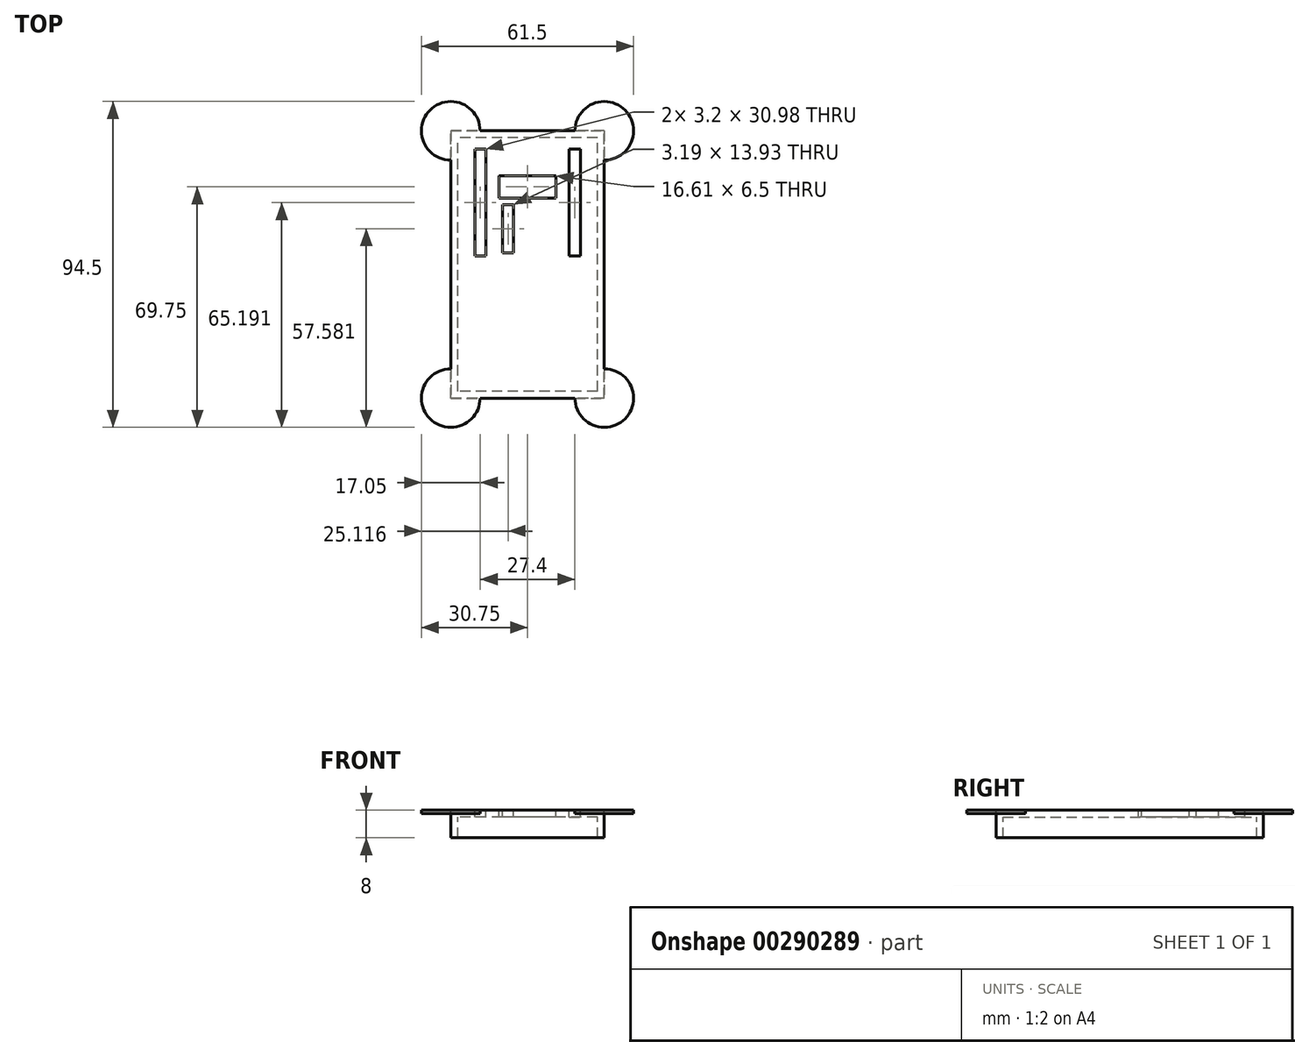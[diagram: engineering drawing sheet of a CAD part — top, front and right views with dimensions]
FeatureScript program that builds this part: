
annotation { "Feature Type Name" : "Feature", "Feature Type Description" : "" }
export const myFeature = defineFeature(function(context is Context, id is Id, definition is map)
    precondition{}
    {
        {
            var Q0;
            Q0=qCreatedBy(makeId("Top.planeOp"),FACE);
            var sketch = newSketch(context, id + "F0", { "sketchPlane" : qUnion([Q0])});
            skLineSegment(sketch, "E0.bottom", {"start": v(20.25, 36.75) * mm, "end": v(-20.25, 36.75) * mm});
            skLineSegment(sketch, "E0.top", {"start": v(20.25, -36.75) * mm, "end": v(-20.25, -36.75) * mm});
            skLineSegment(sketch, "E0.left", {"start": v(20.25, 36.75) * mm, "end": v(20.25, -36.75) * mm});
            skLineSegment(sketch, "E0.right", {"start": v(-20.25, 36.75) * mm, "end": v(-20.25, -36.75) * mm});
            skPoint(sketch, "E0.middle", {"position": v(0, 0) * mm});
            skLineSegment(sketch, "E1.bottom", {"start": v(22.25, 38.75) * mm, "end": v(-22.25, 38.75) * mm});
            skLineSegment(sketch, "E1.top", {"start": v(22.25, -38.75) * mm, "end": v(-22.25, -38.75) * mm});
            skLineSegment(sketch, "E1.left", {"start": v(22.25, 38.75) * mm, "end": v(22.25, -38.75) * mm});
            skLineSegment(sketch, "E1.right", {"start": v(-22.25, 38.75) * mm, "end": v(-22.25, -38.75) * mm});
            skLineSegment(sketch, "E2.bottom", {"start": v(17.1, 34.25) * mm, "end": v(-17.1, 34.25) * mm});
            skLineSegment(sketch, "E2.top", {"start": v(17.1, 0.75) * mm, "end": v(-17.1, 0.75) * mm});
            skLineSegment(sketch, "E2.left", {"start": v(17.1, 34.25) * mm, "end": v(17.1, 0.75) * mm});
            skLineSegment(sketch, "E2.right", {"start": v(-17.1, 34.25) * mm, "end": v(-17.1, 0.75) * mm});
            skPoint(sketch, "E2.middle", {"position": v(0, 17.5) * mm});
            skLineSegment(sketch, "E3.bottom", {"start": v(12.1, 33.43) * mm, "end": v(15.3, 33.43) * mm});
            skLineSegment(sketch, "E3.top", {"start": v(12.1, 2.45) * mm, "end": v(15.3, 2.45) * mm});
            skLineSegment(sketch, "E3.left", {"start": v(12.1, 33.43) * mm, "end": v(12.1, 2.45) * mm});
            skLineSegment(sketch, "E3.right", {"start": v(15.3, 33.43) * mm, "end": v(15.3, 2.45) * mm});
            skLineSegment(sketch, "E4", {"start": v(0, 34.25) * mm, "end": v(0, 0.75) * mm, "construction": true});
            skLineSegment(sketch, "E5.MirrorCS", {"start": v(-12.1, 33.43) * mm, "end": v(-12.1, 2.45) * mm});
            skLineSegment(sketch, "E6.MirrorCS", {"start": v(-12.1, 33.43) * mm, "end": v(-15.3, 33.43) * mm});
            skLineSegment(sketch, "E7.MirrorCS", {"start": v(-15.3, 33.43) * mm, "end": v(-15.3, 2.45) * mm});
            skLineSegment(sketch, "E8.MirrorCS", {"start": v(-12.1, 2.45) * mm, "end": v(-15.3, 2.45) * mm});
            skLineSegment(sketch, "E9.bottom", {"start": v(8.3, 25.75) * mm, "end": v(-8.3, 25.75) * mm});
            skLineSegment(sketch, "E9.top", {"start": v(8.3, 19.25) * mm, "end": v(-8.3, 19.25) * mm});
            skLineSegment(sketch, "E9.left", {"start": v(8.3, 25.75) * mm, "end": v(8.3, 19.25) * mm});
            skLineSegment(sketch, "E9.right", {"start": v(-8.3, 25.75) * mm, "end": v(-8.3, 19.25) * mm});
            skPoint(sketch, "E9.middle", {"position": v(0, 22.5) * mm});
            skLineSegment(sketch, "E10.bottom", {"start": v(-4.04, 17.3) * mm, "end": v(-7.23, 17.3) * mm});
            skLineSegment(sketch, "E10.top", {"start": v(-4.04, 3.37) * mm, "end": v(-7.23, 3.37) * mm});
            skLineSegment(sketch, "E10.left", {"start": v(-4.04, 17.3) * mm, "end": v(-4.04, 3.37) * mm});
            skLineSegment(sketch, "E10.right", {"start": v(-7.23, 17.3) * mm, "end": v(-7.23, 3.37) * mm});
            skPoint(sketch, "E10.middle", {"position": v(-5.63, 10.33) * mm});
            skSolve(sketch);
        }
        {
            var Q0;
            Q0=makeQuery(id+"F0.imprint","IMPRINT",FACE,{"disambiguationData":[TD([[makeQuery(id+"F0.imprint","IMPRINT",EDGE,{"derivedFrom":sQuery(id+"F0.wireOp",EDGE,"E0.bottom")}),1.0]])]});
            var Q1;
            Q1=makeQuery(id+"F0.imprint","IMPRINT",FACE,{"disambiguationData":[TD([[makeQuery(id+"F0.imprint","IMPRINT",EDGE,{"derivedFrom":sQuery(id+"F0.wireOp",EDGE,"E0.bottom")}),-1.0]])]});
            var Q2;
            Q2=makeQuery(id+"F0.imprint","IMPRINT",FACE,{"disambiguationData":[TD([[makeQuery(id+"F0.imprint","IMPRINT",EDGE,{"derivedFrom":sQuery(id+"F0.wireOp",EDGE,"E2.bottom")}),1.0]])]});
            extrude(context, id + "F1", {"entities" : qUnion([Q0, Q1, Q2]), "oppositeDirection" : true, "depth" : 2 * mm});
        }
        {
            var Q0;
            Q0=makeQuery(id+"F1.opExtrude","CAP_FACE",FACE,{"disambiguationData":[OSD([sQuery(id+"F0.wireOp",EDGE,"E1.bottom"),sQuery(id+"F0.wireOp",EDGE,"E1.top"),sQuery(id+"F0.wireOp",EDGE,"E1.left"),sQuery(id+"F0.wireOp",EDGE,"E1.right")])],"isStart":false});
            var sketch = newSketch(context, id + "F2", { "sketchPlane" : qUnion([Q0])});
            skLineSegment(sketch, "E11.bottom", {"start": v(-22.25, 38.75) * mm, "end": v(22.25, 38.75) * mm});
            skLineSegment(sketch, "E11.top", {"start": v(-22.25, -38.75) * mm, "end": v(22.25, -38.75) * mm});
            skLineSegment(sketch, "E11.left", {"start": v(-22.25, 38.75) * mm, "end": v(-22.25, -38.75) * mm});
            skLineSegment(sketch, "E11.right", {"start": v(22.25, 38.75) * mm, "end": v(22.25, -38.75) * mm});
            skLineSegment(sketch, "E12.bottom", {"start": v(20.25, 36.75) * mm, "end": v(-20.25, 36.75) * mm});
            skLineSegment(sketch, "E12.top", {"start": v(20.25, -36.75) * mm, "end": v(-20.25, -36.75) * mm});
            skLineSegment(sketch, "E12.left", {"start": v(20.25, 36.75) * mm, "end": v(20.25, -36.75) * mm});
            skLineSegment(sketch, "E12.right", {"start": v(-20.25, 36.75) * mm, "end": v(-20.25, -36.75) * mm});
            skPoint(sketch, "E12.middle", {"position": v(0, 0) * mm});
            skSolve(sketch);
        }
        {
            var Q0;
            Q0=makeQuery(id+"F2.imprint","IMPRINT",FACE,{"disambiguationData":[TD([[makeQuery(id+"F2.imprint","IMPRINT",EDGE,{"derivedFrom":sQuery(id+"F2.wireOp",EDGE,"E11.bottom")}),1.0]])]});
            extrude(context, id + "F3", {"entities" : qUnion([Q0]), "operationType" : NewBodyOperationType.ADD, "depth" : 6 * mm});
        }
        {
            var Q0;
            Q0=makeQuery(id+"F1.opExtrude","CAP_FACE",FACE,{"disambiguationData":[OSD([sQuery(id+"F0.wireOp",EDGE,"E1.bottom"),sQuery(id+"F0.wireOp",EDGE,"E1.top"),sQuery(id+"F0.wireOp",EDGE,"E1.left"),sQuery(id+"F0.wireOp",EDGE,"E1.right"),sQuery(id+"F0.wireOp",EDGE,"E3.bottom"),sQuery(id+"F0.wireOp",EDGE,"E3.top"),sQuery(id+"F0.wireOp",EDGE,"E3.left"),sQuery(id+"F0.wireOp",EDGE,"E3.right"),sQuery(id+"F0.wireOp",EDGE,"E5.MirrorCS"),sQuery(id+"F0.wireOp",EDGE,"E6.MirrorCS"),sQuery(id+"F0.wireOp",EDGE,"E7.MirrorCS"),sQuery(id+"F0.wireOp",EDGE,"E8.MirrorCS"),sQuery(id+"F0.wireOp",EDGE,"E9.bottom"),sQuery(id+"F0.wireOp",EDGE,"E9.top"),sQuery(id+"F0.wireOp",EDGE,"E9.left"),sQuery(id+"F0.wireOp",EDGE,"E9.right"),sQuery(id+"F0.wireOp",EDGE,"E10.bottom"),sQuery(id+"F0.wireOp",EDGE,"E10.top"),sQuery(id+"F0.wireOp",EDGE,"E10.left"),sQuery(id+"F0.wireOp",EDGE,"E10.right")])],"isStart":true});
            var sketch = newSketch(context, id + "F4", { "sketchPlane" : qUnion([Q0])});
            skCircle(sketch, "E13", {"center": v(-22.25, 38.75) * mm, "radius": 8.5 * mm});
            skCircle(sketch, "E14", {"center": v(22.25, 38.75) * mm, "radius": 8.5 * mm});
            skCircle(sketch, "E15", {"center": v(22.25, -38.75) * mm, "radius": 8.5 * mm});
            skCircle(sketch, "E16", {"center": v(-22.25, -38.75) * mm, "radius": 8.5 * mm});
            skSolve(sketch);
        }
        {
            var Q0;
            Q0 = qSketchRegion(id + "F4", true);
            extrude(context, id + "F5", {"entities" : qUnion([Q0]), "operationType" : NewBodyOperationType.ADD, "oppositeDirection" : true, "depth" : 1 * mm});
        }
    });
